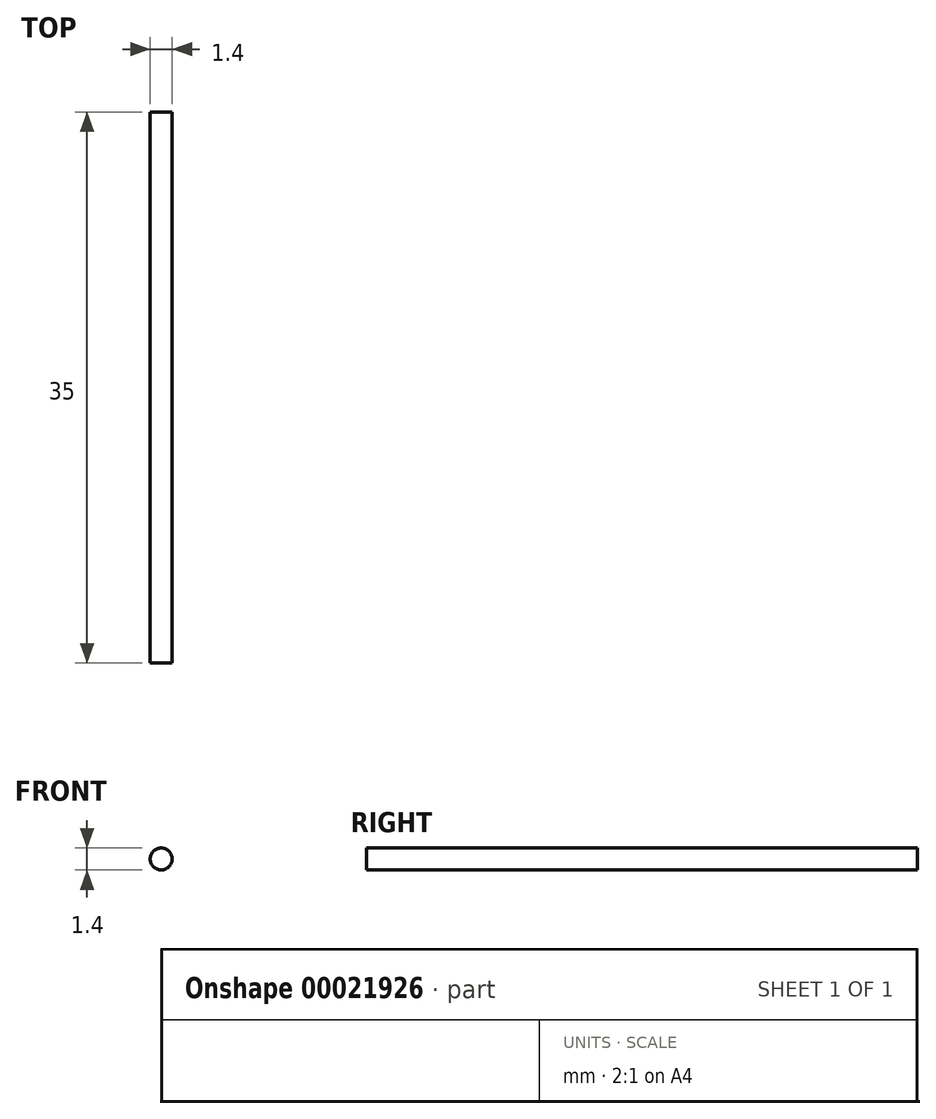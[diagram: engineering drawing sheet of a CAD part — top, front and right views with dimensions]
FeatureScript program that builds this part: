
annotation { "Feature Type Name" : "Feature", "Feature Type Description" : "" }
export const myFeature = defineFeature(function(context is Context, id is Id, definition is map)
    precondition{}
    {
        {
            var Q0;
            Q0=qCreatedBy(makeId("Front.planeOp"),FACE);
            var sketch = newSketch(context, id + "F0", { "sketchPlane" : qUnion([Q0])});
            skCircle(sketch, "E0", {"center": v(0, 0) * mm, "radius": 0.7 * mm});
            skSolve(sketch);
        }
        {
            var Q0;
            Q0=makeQuery(id+"F0.imprint","IMPRINT",FACE,{"disambiguationData":[TD([[makeQuery(id+"F0.imprint","IMPRINT",EDGE,{"derivedFrom":sQuery(id+"F0.wireOp",EDGE,"E0")}),1.0]])]});
            extrude(context, id + "F1", {"entities" : qUnion([Q0]), "depth" : 35 * mm});
        }
    });
